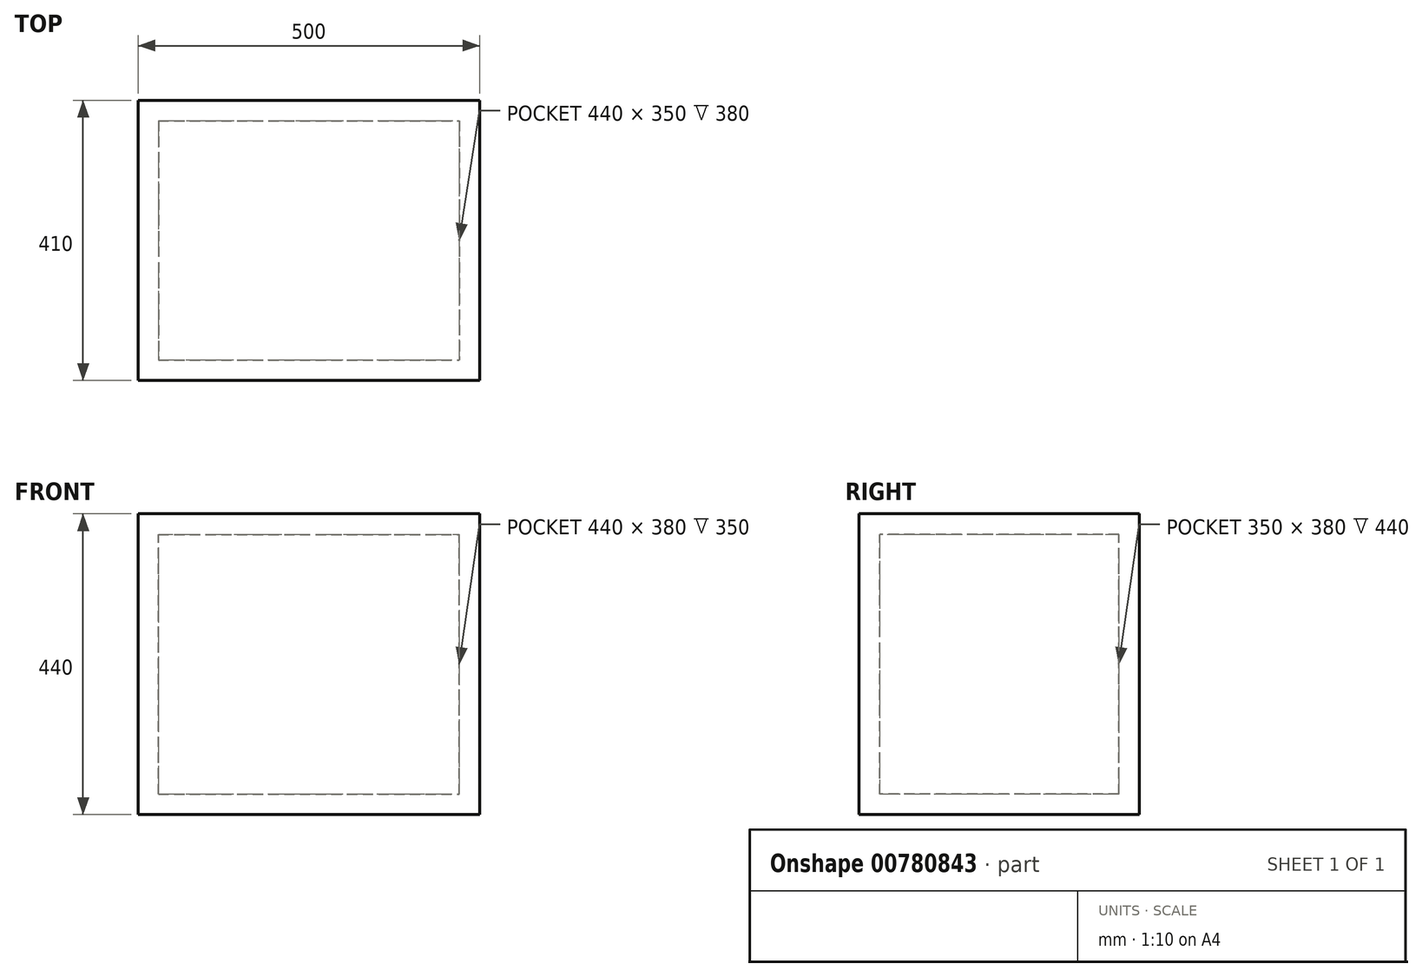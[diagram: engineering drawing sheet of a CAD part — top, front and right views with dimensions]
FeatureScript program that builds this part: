
annotation { "Feature Type Name" : "Feature", "Feature Type Description" : "" }
export const myFeature = defineFeature(function(context is Context, id is Id, definition is map)
    precondition{}
    {
        {
            var Q0;
            Q0=qCreatedBy(makeId("Front.planeOp"),FACE);
            var sketch = newSketch(context, id + "F0", { "sketchPlane" : qUnion([Q0])});
            skLineSegment(sketch, "E0.bottom", {"start": v(-250, -205) * mm, "end": v(250, -205) * mm});
            skLineSegment(sketch, "E0.top", {"start": v(-250, 205) * mm, "end": v(250, 205) * mm});
            skLineSegment(sketch, "E0.left", {"start": v(-250, -205) * mm, "end": v(-250, 205) * mm});
            skLineSegment(sketch, "E0.right", {"start": v(250, -205) * mm, "end": v(250, 205) * mm});
            skPoint(sketch, "E0.middle", {"position": v(0, 0) * mm});
            skSolve(sketch);
        }
        {
            var Q0;
            Q0=makeQuery(id+"F0.imprint","IMPRINT",FACE,{"disambiguationData":[TD([[makeQuery(id+"F0.imprint","IMPRINT",EDGE,{"derivedFrom":sQuery(id+"F0.wireOp",EDGE,"E0.bottom")}),1.0]])]});
            extrude(context, id + "F1", {"entities" : qUnion([Q0]), "oppositeDirection" : true, "depth" : 410 * mm, "offsetDistance" : 25 * mm});
        }
        {
            var Q0;
            Q0=makeQuery(id+"F1.opExtrude","SWEPT_FACE",FACE,{"disambiguationData":[OSD([sQuery(id+"F0.wireOp",EDGE,"E0.top")])]});
            shell(context, id + "F2", {"entities" : qUnion([Q0]), "thickness" : 30 * mm});
        }
        {
            var Q0;
            Q0=makeQuery(id+"F1.opExtrude","SWEPT_FACE",FACE,{"disambiguationData":[OSD([sQuery(id+"F0.wireOp",EDGE,"E0.top")])]});
            var sketch = newSketch(context, id + "F3", { "sketchPlane" : qUnion([Q0])});
            skLineSegment(sketch, "E1.bottom", {"start": v(-250, 0) * mm, "end": v(250, 0) * mm});
            skLineSegment(sketch, "E1.top", {"start": v(-250, 410) * mm, "end": v(250, 410) * mm});
            skLineSegment(sketch, "E1.left", {"start": v(-250, 0) * mm, "end": v(-250, 410) * mm});
            skLineSegment(sketch, "E1.right", {"start": v(250, 0) * mm, "end": v(250, 410) * mm});
            skSolve(sketch);
        }
        {
            var Q0;
            Q0 = qSketchRegion(id + "F3", true);
            extrude(context, id + "F4", {"entities" : qUnion([Q0]), "operationType" : NewBodyOperationType.ADD, "depth" : 30 * mm, "offsetDistance" : 25 * mm});
        }
    });
